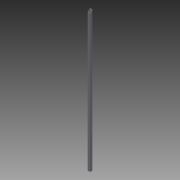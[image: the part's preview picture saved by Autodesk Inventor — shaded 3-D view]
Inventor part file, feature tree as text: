
AUTODESK INVENTOR PART (.ipt)
format: ipt  version: 2015 SP1 (Build 190203100, 203)  size: 83,456 bytes
history: native  units: mm
features: other x3, sketch x3
ambient origin geometry x8: Origin, YZ Plane, XZ Plane, XY Plane, X Axis, Y Axis, Z Axis, Center Point
bodies: Solid1 (feature_tree)
feature tree (6):
  other  "Poutre.ipt"
  other  "Solid1::Poutre.ipt"
  other  "TaggingFeature1"
  sketch  "Sketch1"  dims[d0=10.0mm]
  sketch  "Sketch2"
  sketch  "Sketch3"
